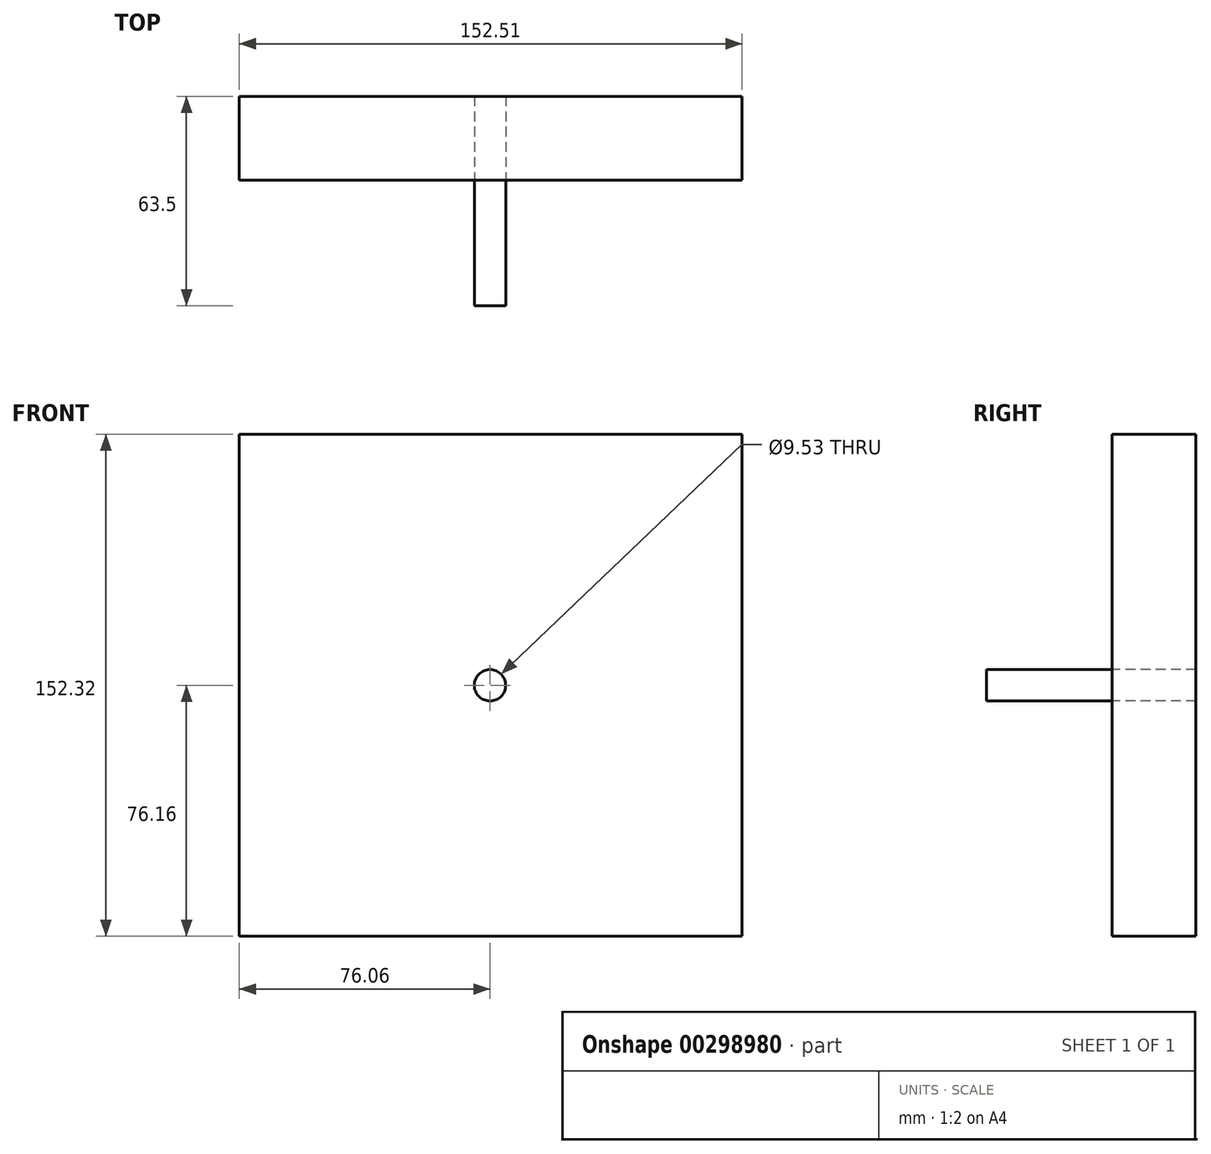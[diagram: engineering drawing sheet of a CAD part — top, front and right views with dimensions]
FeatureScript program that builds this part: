
annotation { "Feature Type Name" : "Feature", "Feature Type Description" : "" }
export const myFeature = defineFeature(function(context is Context, id is Id, definition is map)
    precondition{}
    {
        {
            var Q0;
            Q0=qCreatedBy(makeId("Front.planeOp"),FACE);
            var sketch = newSketch(context, id + "F0", { "sketchPlane" : qUnion([Q0])});
            skLineSegment(sketch, "E0.bottom", {"start": v(-76.06, 76.16) * mm, "end": v(76.45, 76.16) * mm});
            skLineSegment(sketch, "E0.top", {"start": v(-76.06, -76.16) * mm, "end": v(76.45, -76.16) * mm});
            skLineSegment(sketch, "E0.left", {"start": v(-76.06, 76.16) * mm, "end": v(-76.06, -76.16) * mm});
            skLineSegment(sketch, "E0.right", {"start": v(76.45, 76.16) * mm, "end": v(76.45, -76.16) * mm});
            skCircle(sketch, "E1", {"center": v(0, 0) * mm, "radius": 4.76 * mm});
            skSolve(sketch);
        }
        {
            var Q0;
            Q0=makeQuery(id+"F0.imprint","IMPRINT",FACE,{"disambiguationData":[TD([[makeQuery(id+"F0.imprint","IMPRINT",EDGE,{"derivedFrom":sQuery(id+"F0.wireOp",EDGE,"E1")}),1.0]])]});
            extrude(context, id + "F1", {"entities" : qUnion([Q0]), "depth" : 25.4 * mm});
        }
        {
            var Q0;
            Q0 = qSketchRegion(id + "F0", true);
            extrude(context, id + "F2", {"entities" : qUnion([Q0]), "operationType" : NewBodyOperationType.ADD, "oppositeDirection" : true, "depth" : 25.4 * mm});
        }
        {
            var Q0;
            Q0=makeQuery(id+"F1.opExtrude","CAP_FACE",FACE,{"disambiguationData":[OSD([sQuery(id+"F0.wireOp",EDGE,"E1")])],"isStart":false});
            extrude(context, id + "F3", {"entities" : qUnion([Q0]), "operationType" : NewBodyOperationType.ADD, "depth" : 12.7 * mm});
        }
    });
